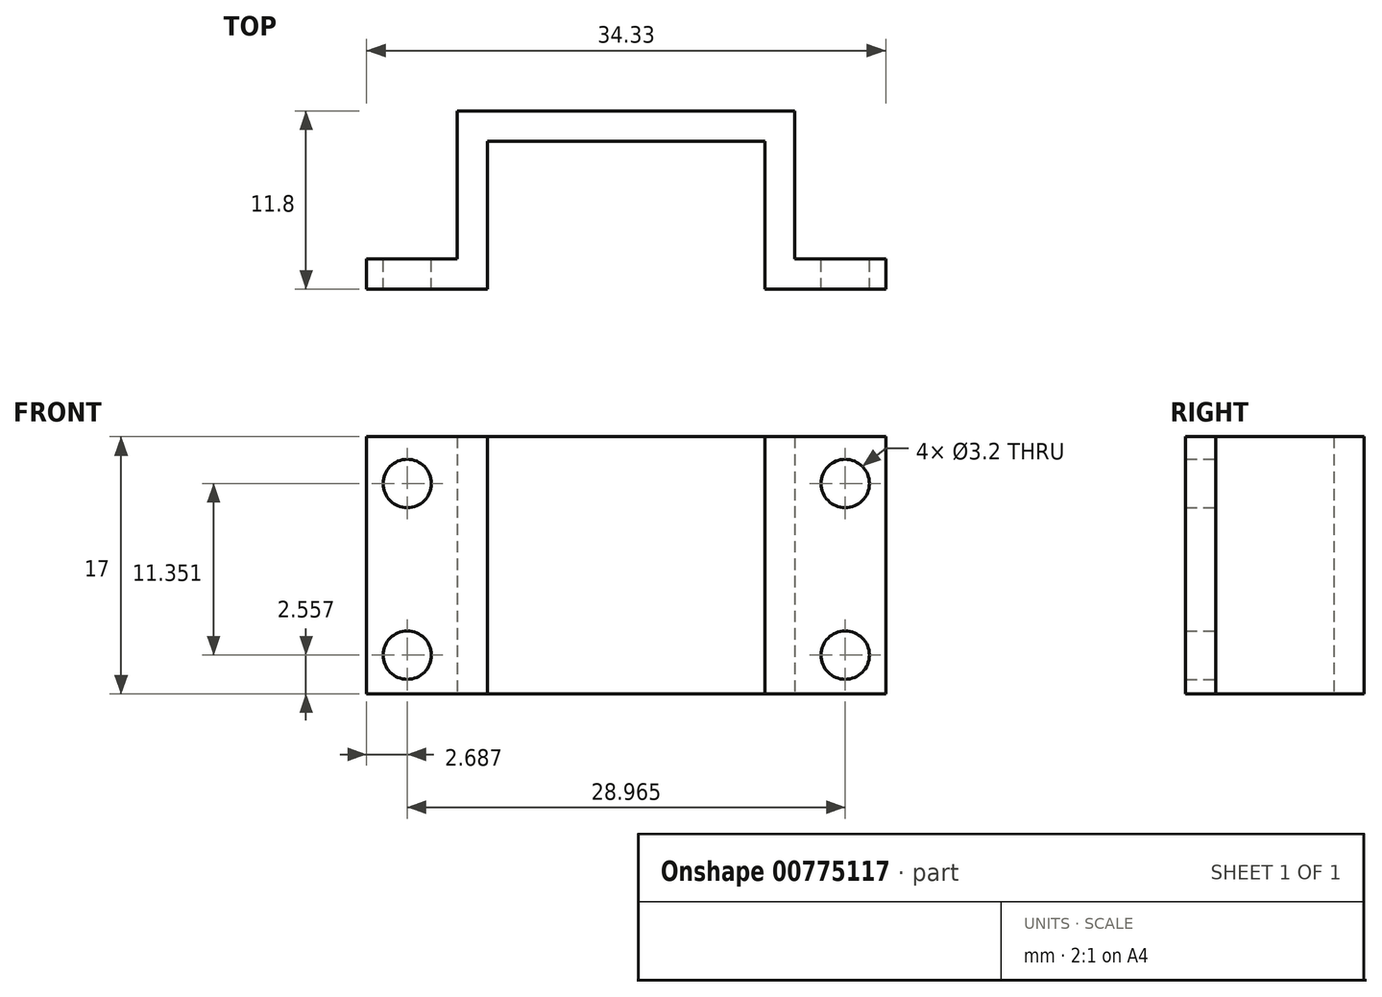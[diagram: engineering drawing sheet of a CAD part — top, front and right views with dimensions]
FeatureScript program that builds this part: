
annotation { "Feature Type Name" : "Feature", "Feature Type Description" : "" }
export const myFeature = defineFeature(function(context is Context, id is Id, definition is map)
    precondition{}
    {
        {
            var Q0;
            Q0=qCreatedBy(makeId("Top.planeOp"),FACE);
            var sketch = newSketch(context, id + "F0", { "sketchPlane" : qUnion([Q0])});
            skLineSegment(sketch, "E0.bottom", {"start": v(-11.15, 35.25) * mm, "end": v(11.15, 35.25) * mm});
            skLineSegment(sketch, "E0.top", {"start": v(-11.15, 37.25) * mm, "end": v(11.15, 37.25) * mm});
            skLineSegment(sketch, "E0.left", {"start": v(-11.15, 35.25) * mm, "end": v(-11.15, 37.25) * mm});
            skLineSegment(sketch, "E0.right", {"start": v(11.15, 35.25) * mm, "end": v(11.15, 37.25) * mm});
            skPoint(sketch, "E0.middle", {"position": v(0, 36.25) * mm});
            skLineSegment(sketch, "E1.bottom", {"start": v(-11.15, 37.25) * mm, "end": v(-9.15, 37.25) * mm});
            skLineSegment(sketch, "E1.top", {"start": v(-11.15, 25.45) * mm, "end": v(-9.15, 25.45) * mm});
            skLineSegment(sketch, "E1.left", {"start": v(-11.15, 37.25) * mm, "end": v(-11.15, 25.45) * mm});
            skLineSegment(sketch, "E1.right", {"start": v(-9.15, 37.25) * mm, "end": v(-9.15, 25.45) * mm});
            skLineSegment(sketch, "E2.bottom", {"start": v(11.15, 37.25) * mm, "end": v(9.18, 37.25) * mm});
            skLineSegment(sketch, "E2.top", {"start": v(11.15, 25.45) * mm, "end": v(9.18, 25.45) * mm});
            skLineSegment(sketch, "E2.left", {"start": v(11.15, 37.25) * mm, "end": v(11.15, 25.45) * mm});
            skLineSegment(sketch, "E2.right", {"start": v(9.18, 37.25) * mm, "end": v(9.18, 25.45) * mm});
            skLineSegment(sketch, "E3.bottom", {"start": v(9.18, 25.45) * mm, "end": v(17.18, 25.45) * mm});
            skLineSegment(sketch, "E3.top", {"start": v(9.18, 27.45) * mm, "end": v(17.18, 27.45) * mm});
            skLineSegment(sketch, "E3.left", {"start": v(9.18, 25.45) * mm, "end": v(9.18, 27.45) * mm});
            skLineSegment(sketch, "E3.right", {"start": v(17.18, 25.45) * mm, "end": v(17.18, 27.45) * mm});
            skLineSegment(sketch, "E4.bottom", {"start": v(-9.15, 25.45) * mm, "end": v(-17.15, 25.45) * mm});
            skLineSegment(sketch, "E4.top", {"start": v(-9.15, 27.45) * mm, "end": v(-17.15, 27.45) * mm});
            skLineSegment(sketch, "E4.left", {"start": v(-9.15, 25.45) * mm, "end": v(-9.15, 27.45) * mm});
            skLineSegment(sketch, "E4.right", {"start": v(-17.15, 25.45) * mm, "end": v(-17.15, 27.45) * mm});
            skSolve(sketch);
        }
        {
            var Q0;
            {var subQ0=sQuery(id+"F0.wireOp",EDGE,"E4.bottom");Q0=makeQuery(id+"F0.imprint","IMPRINT",FACE,{"disambiguationData":[TD([[makeQuery(id+"F0.imprint","IMPRINT",EDGE,{"derivedFrom":subQ0}),-1.0]])]});}
            var Q1;
            {var subQ0=sQuery(id+"F0.wireOp",EDGE,"E1.top");Q1=makeQuery(id+"F0.imprint","IMPRINT",FACE,{"disambiguationData":[TD([[makeQuery(id+"F0.imprint","IMPRINT",EDGE,{"derivedFrom":subQ0}),1.0]])]});}
            var Q2;
            {var subQ0=sQuery(id+"F0.wireOp",EDGE,"E1.right");var subQ1=sQuery(id+"F0.wireOp",EDGE,"E0.bottom");var subQ2=makeQuery(id+"F0.imprint","INTERSECT",VERTEX,{"derivedFrom":[subQ1,subQ0]});Q2=makeQuery(id+"F0.imprint","IMPRINT",FACE,{"disambiguationData":[TD([[makeQuery(id+"F0.imprint","IMPRINT",EDGE,{"disambiguationData":[TD([[subQ2,-1.0]])],"derivedFrom":subQ0}),-1.0]])]});}
            var Q3;
            {var subQ3=sQuery(id+"F0.wireOp",EDGE,"E0.left");Q3=makeQuery(id+"F0.imprint","IMPRINT",FACE,{"disambiguationData":[TD([[makeQuery(id+"F0.imprint","IMPRINT",EDGE,{"derivedFrom":subQ3}),-1.0]])]});}
            var Q4;
            {var subQ0=sQuery(id+"F0.wireOp",EDGE,"E1.right");var subQ1=sQuery(id+"F0.wireOp",EDGE,"E0.bottom");var subQ2=makeQuery(id+"F0.imprint","INTERSECT",VERTEX,{"derivedFrom":[subQ1,subQ0]});Q4=makeQuery(id+"F0.imprint","IMPRINT",FACE,{"disambiguationData":[TD([[makeQuery(id+"F0.imprint","IMPRINT",EDGE,{"disambiguationData":[TD([[subQ2,-1.0]])],"derivedFrom":subQ1}),1.0]])]});}
            var Q5;
            {var subQ0=sQuery(id+"F0.wireOp",EDGE,"E0.right");Q5=makeQuery(id+"F0.imprint","IMPRINT",FACE,{"disambiguationData":[TD([[makeQuery(id+"F0.imprint","IMPRINT",EDGE,{"derivedFrom":subQ0}),1.0]])]});}
            var Q6;
            {var subQ1=sQuery(id+"F0.wireOp",EDGE,"E0.bottom");var subQ3=sQuery(id+"F0.wireOp",EDGE,"E2.right");var subQ4=makeQuery(id+"F0.imprint","INTERSECT",VERTEX,{"derivedFrom":[subQ1,subQ3]});Q6=makeQuery(id+"F0.imprint","IMPRINT",FACE,{"disambiguationData":[TD([[makeQuery(id+"F0.imprint","IMPRINT",EDGE,{"disambiguationData":[TD([[subQ4,-1.0]])],"derivedFrom":subQ3}),1.0]])]});}
            var Q7;
            {var subQ0=sQuery(id+"F0.wireOp",EDGE,"E2.top");Q7=makeQuery(id+"F0.imprint","IMPRINT",FACE,{"disambiguationData":[TD([[makeQuery(id+"F0.imprint","IMPRINT",EDGE,{"derivedFrom":subQ0}),-1.0]])]});}
            var Q8;
            {var subQ0=sQuery(id+"F0.wireOp",EDGE,"E3.bottom");Q8=makeQuery(id+"F0.imprint","IMPRINT",FACE,{"disambiguationData":[TD([[makeQuery(id+"F0.imprint","IMPRINT",EDGE,{"derivedFrom":subQ0}),1.0]])]});}
            extrude(context, id + "F1", {"entities" : qUnion([Q0, Q1, Q2, Q3, Q4, Q5, Q6, Q7, Q8]), "depth" : 17 * mm, "offsetDistance" : 25 * mm});
        }
        {
            var Q0;
            Q0=makeQuery(id+"F1.opExtrude","SWEPT_FACE",FACE,{"disambiguationData":[OSD([sQuery(id+"F0.wireOp",EDGE,"E3.top")])]});
            var sketch = newSketch(context, id + "F2", { "sketchPlane" : qUnion([Q0])});
            skCircle(sketch, "E5", {"center": v(-14.5, 13.9) * mm, "radius": 1.55 * mm});
            skCircle(sketch, "E6", {"center": v(-14.5, 2.56) * mm, "radius": 1.55 * mm});
            skCircle(sketch, "E7", {"center": v(14.46, 2.56) * mm, "radius": 1.55 * mm});
            skCircle(sketch, "E8", {"center": v(14.46, 13.9) * mm, "radius": 1.55 * mm});
            skSolve(sketch);
        }
        {
            var Q0;
            Q0=sQuery(id+"F2.wireOp",VERTEX,"E5.center");
            var Q1;
            Q1=sQuery(id+"F2.wireOp",VERTEX,"E6.center");
            var Q2;
            Q2=sQuery(id+"F2.wireOp",VERTEX,"E7.center");
            var Q3;
            Q3=sQuery(id+"F2.wireOp",VERTEX,"E8.center");
            var Q4;
            Q4=makeQuery(id+"F1.opExtrude","SWEPT_BODY",BODY,{"disambiguationData":[OSD([sQuery(id+"F0.wireOp",EDGE,"E0.bottom"),sQuery(id+"F0.wireOp",EDGE,"E0.top"),sQuery(id+"F0.wireOp",EDGE,"E0.left"),sQuery(id+"F0.wireOp",EDGE,"E0.right"),sQuery(id+"F0.wireOp",EDGE,"E1.top"),sQuery(id+"F0.wireOp",EDGE,"E1.left"),sQuery(id+"F0.wireOp",EDGE,"E1.right"),sQuery(id+"F0.wireOp",EDGE,"E2.top"),sQuery(id+"F0.wireOp",EDGE,"E2.left"),sQuery(id+"F0.wireOp",EDGE,"E2.right"),sQuery(id+"F0.wireOp",EDGE,"E3.bottom"),sQuery(id+"F0.wireOp",EDGE,"E3.top"),sQuery(id+"F0.wireOp",EDGE,"E3.right"),sQuery(id+"F0.wireOp",EDGE,"E4.bottom"),sQuery(id+"F0.wireOp",EDGE,"E4.top"),sQuery(id+"F0.wireOp",EDGE,"E4.right")])]});
            hole(context, id + "F3", {"style" : HoleStyle.SIMPLE, "endStyle" : HoleEndStyle.THROUGH, "holeDiameter" : 3.2 * mm, "majorDiameter" : 5 * mm, "isTappedThrough" : true, "tappedDepth" : 12 * mm, "tapClearance" : 3, "locations" : qUnion([Q0, Q1, Q2, Q3]), "scope" : qUnion([Q4])});
        }
    });
